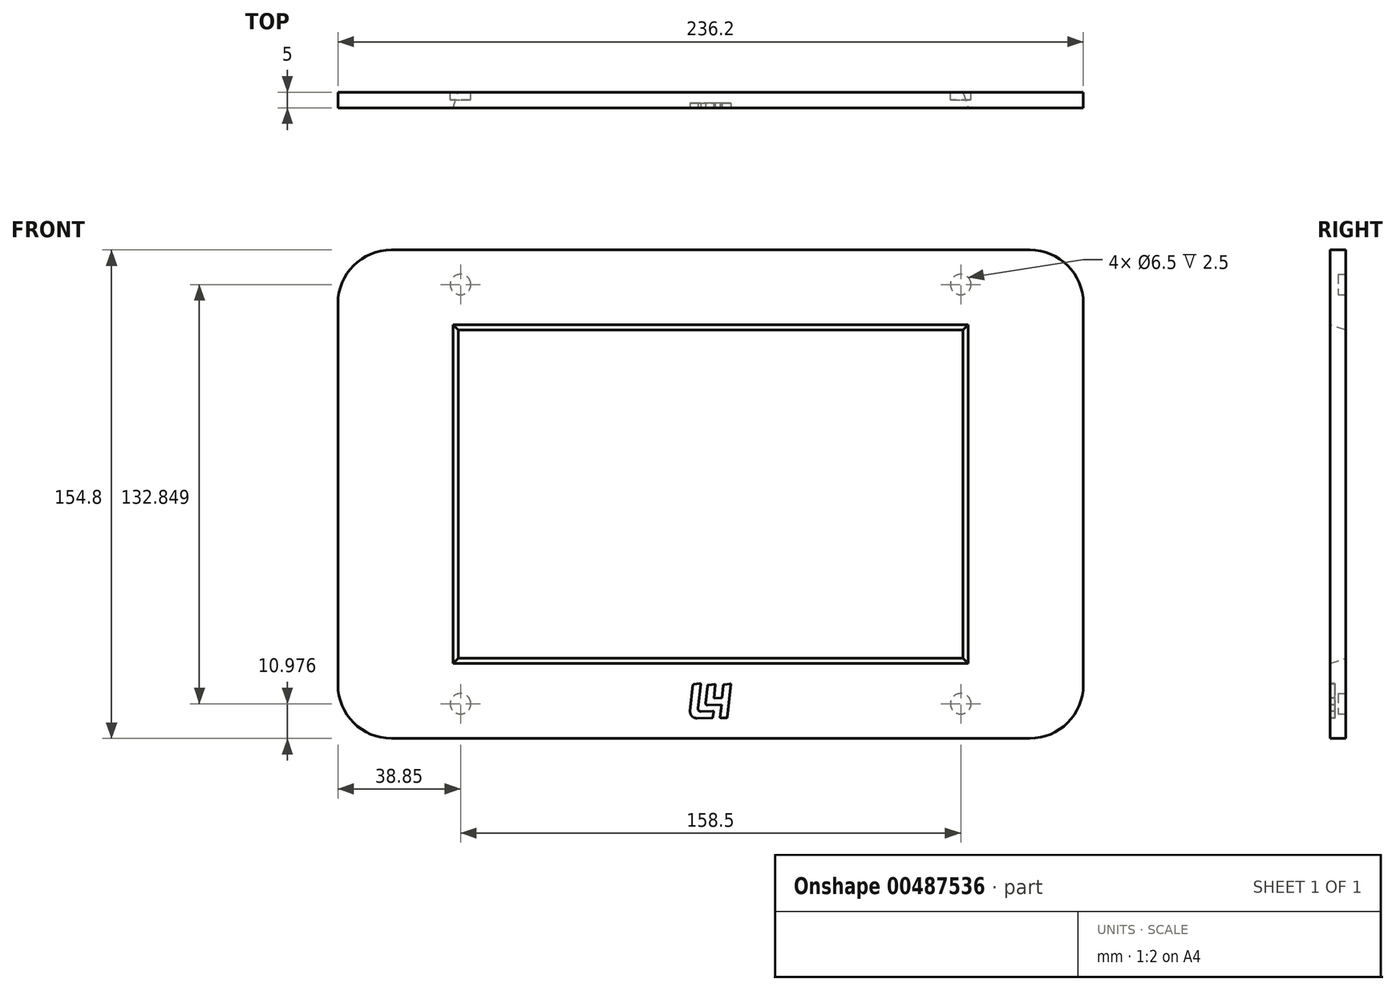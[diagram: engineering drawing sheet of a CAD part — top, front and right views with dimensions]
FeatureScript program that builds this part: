
annotation { "Feature Type Name" : "Feature", "Feature Type Description" : "" }
export const myFeature = defineFeature(function(context is Context, id is Id, definition is map)
    precondition{}
    {
        {
            var Q0;
            Q0=qCreatedBy(makeId("Front.planeOp"),FACE);
            var sketch = newSketch(context, id + "F0", { "sketchPlane" : qUnion([Q0])});
            skLineSegment(sketch, "E0.bottom", {"start": v(-80, 52) * mm, "end": v(80, 52) * mm});
            skLineSegment(sketch, "E0.top", {"start": v(-80, -52) * mm, "end": v(80, -52) * mm});
            skLineSegment(sketch, "E0.left", {"start": v(-80, 52) * mm, "end": v(-80, -52) * mm});
            skLineSegment(sketch, "E0.right", {"start": v(80, 52) * mm, "end": v(80, -52) * mm});
            skPoint(sketch, "E0.middle", {"position": v(0, 0) * mm});
            skLineSegment(sketch, "E1.bottom", {"start": v(-118.1, 77.4) * mm, "end": v(118.1, 77.4) * mm});
            skLineSegment(sketch, "E1.top", {"start": v(-118.1, -77.4) * mm, "end": v(118.1, -77.4) * mm});
            skLineSegment(sketch, "E1.left", {"start": v(-118.1, 77.4) * mm, "end": v(-118.1, -77.4) * mm});
            skLineSegment(sketch, "E1.right", {"start": v(118.1, 77.4) * mm, "end": v(118.1, -77.4) * mm});
            skSolve(sketch);
        }
        {
            var Q0;
            Q0=makeQuery(id+"F0.imprint","IMPRINT",FACE,{"disambiguationData":[TD([[makeQuery(id+"F0.imprint","IMPRINT",EDGE,{"derivedFrom":sQuery(id+"F0.wireOp",EDGE,"E0.bottom")}),1.0]])]});
            extrude(context, id + "F1", {"entities" : qUnion([Q0]), "depth" : 5 * mm});
        }
        {
            var Q0;
            Q0=makeQuery(id+"F1.opExtrude","SWEPT_EDGE",EDGE,{"disambiguationData":[OSD([sQuery(id+"F0.wireOp",EDGE,"E1.bottom"),sQuery(id+"F0.wireOp",EDGE,"E1.left")])]});
            var Q1;
            Q1=makeQuery(id+"F1.opExtrude","SWEPT_EDGE",EDGE,{"disambiguationData":[OSD([sQuery(id+"F0.wireOp",EDGE,"E1.bottom"),sQuery(id+"F0.wireOp",EDGE,"E1.right")])]});
            var Q2;
            Q2=makeQuery(id+"F1.opExtrude","SWEPT_EDGE",EDGE,{"disambiguationData":[OSD([sQuery(id+"F0.wireOp",EDGE,"E1.top"),sQuery(id+"F0.wireOp",EDGE,"E1.left")])]});
            var Q3;
            Q3=makeQuery(id+"F1.opExtrude","SWEPT_EDGE",EDGE,{"disambiguationData":[OSD([sQuery(id+"F0.wireOp",EDGE,"E1.top"),sQuery(id+"F0.wireOp",EDGE,"E1.right")])]});
            fillet(context, id + "F2", {"entities" : qUnion([Q0, Q1, Q2, Q3]), "radius" : 17 * mm, "tangentPropagation" : true, "allowEdgeOverflow" : false});
        }
        {
            var Q0;
            Q0=makeQuery(id+"F1.opExtrude","CAP_FACE",FACE,{"disambiguationData":[OSD([sQuery(id+"F0.wireOp",EDGE,"E0.bottom"),sQuery(id+"F0.wireOp",EDGE,"E0.top"),sQuery(id+"F0.wireOp",EDGE,"E0.left"),sQuery(id+"F0.wireOp",EDGE,"E0.right"),sQuery(id+"F0.wireOp",EDGE,"E1.bottom"),sQuery(id+"F0.wireOp",EDGE,"E1.top"),sQuery(id+"F0.wireOp",EDGE,"E1.left"),sQuery(id+"F0.wireOp",EDGE,"E1.right")])],"isStart":true});
            var sketch = newSketch(context, id + "F3", { "sketchPlane" : qUnion([Q0])});
            skCircle(sketch, "E2", {"center": v(-79.25, 66.42) * mm, "radius": 3.25 * mm});
            skCircle(sketch, "E3.MirrorC", {"center": v(-79.25, -66.42) * mm, "radius": 3.25 * mm});
            skCircle(sketch, "E4.MirrorC", {"center": v(79.25, 66.42) * mm, "radius": 3.25 * mm});
            skCircle(sketch, "E5.MirrorC", {"center": v(79.25, -66.42) * mm, "radius": 3.25 * mm});
            skSolve(sketch);
        }
        {
            var Q0;
            Q0=qSketchRegion(id+"F3",true);
            extrude(context, id + "F4", {"entities" : qUnion([Q0]), "operationType" : NewBodyOperationType.REMOVE, "oppositeDirection" : true, "depth" : 2.5 * mm});
        }
        {
            var Q0;
            Q0=makeQuery(id+"F1.opExtrude","CAP_EDGE",EDGE,{"disambiguationData":[OSD([sQuery(id+"F0.wireOp",EDGE,"E0.left")])],"isStart":false});
            var Q1;
            Q1=makeQuery(id+"F1.opExtrude","CAP_EDGE",EDGE,{"disambiguationData":[OSD([sQuery(id+"F0.wireOp",EDGE,"E0.bottom")])],"isStart":false});
            var Q2;
            Q2=makeQuery(id+"F1.opExtrude","CAP_EDGE",EDGE,{"disambiguationData":[OSD([sQuery(id+"F0.wireOp",EDGE,"E0.right")])],"isStart":false});
            var Q3;
            Q3=makeQuery(id+"F1.opExtrude","CAP_EDGE",EDGE,{"disambiguationData":[OSD([sQuery(id+"F0.wireOp",EDGE,"E0.top")])],"isStart":false});
            chamfer(context, id + "F5", {"entities" : qUnion([Q0, Q1, Q2, Q3]), "chamferType" : ChamferType.OFFSET_ANGLE, "width" : 5 * mm, "oppositeDirection" : false, "angle" : 18 * degree, "tangentPropagation" : true});
        }
        {
            var Q0;
            Q0=makeQuery(id+"F1.opExtrude","CAP_FACE",FACE,{"disambiguationData":[OSD([sQuery(id+"F0.wireOp",EDGE,"E0.bottom"),sQuery(id+"F0.wireOp",EDGE,"E0.top"),sQuery(id+"F0.wireOp",EDGE,"E0.left"),sQuery(id+"F0.wireOp",EDGE,"E0.right"),sQuery(id+"F0.wireOp",EDGE,"E1.bottom"),sQuery(id+"F0.wireOp",EDGE,"E1.top"),sQuery(id+"F0.wireOp",EDGE,"E1.left"),sQuery(id+"F0.wireOp",EDGE,"E1.right")])],"isStart":false});
            var sketch = newSketch(context, id + "F6", { "sketchPlane" : qUnion([Q0])});
            skPoint(sketch, "E6", {"position": v(0, -65.51) * mm});
            skPoint(sketch, "E6.positionSnap0", {"position": v(0, -75.04) * mm});
            skPoint(sketch, "E6.positionSnap1", {"position": v(10.5, -65.51) * mm});
            skLineSegment(sketch, "E7", {"start": v(0, -53.62) * mm, "end": v(0, -77.4) * mm});
            skLineSegment(sketch, "E8", {"start": v(-5.6, -60.55) * mm, "end": v(-6.49, -68.68) * mm});
            skLineSegment(sketch, "E9", {"start": v(-4.35, -71) * mm, "end": v(0.45, -70.9) * mm});
            skLineSegment(sketch, "E10", {"start": v(0.74, -70.63) * mm, "end": v(0.95, -68.94) * mm});
            skLineSegment(sketch, "E11", {"start": v(0.74, -68.71) * mm, "end": v(-3.13, -68.85) * mm});
            skLineSegment(sketch, "E12", {"start": v(-4, -67.9) * mm, "end": v(-3.09, -60.3) * mm});
            skLineSegment(sketch, "E13", {"start": v(-3.37, -60.02) * mm, "end": v(-5.35, -60.28) * mm});
            skPoint(sketch, "E14.visualSharp", {"position": v(-5.58, -60.32) * mm});
            skArc(sketch, "E14.filletArc", {"start": v(-5.35, -60.28) * mm, "mid": v(-5.52, -60.37) * mm, "end": v(-5.6, -60.55) * mm});
            skPoint(sketch, "E15.visualSharp", {"position": v(-3.05, -59.98) * mm});
            skArc(sketch, "E15.filletArc", {"start": v(-3.09, -60.3) * mm, "mid": v(-3.16, -60.1) * mm, "end": v(-3.37, -60.02) * mm});
            skPoint(sketch, "E16.visualSharp", {"position": v(-6.74, -71.06) * mm});
            skArc(sketch, "E16.filletArc", {"start": v(-6.49, -68.68) * mm, "mid": v(-5.95, -70.33) * mm, "end": v(-4.35, -71) * mm});
            skPoint(sketch, "E17.visualSharp", {"position": v(0.98, -68.7) * mm});
            skArc(sketch, "E17.filletArc", {"start": v(0.95, -68.94) * mm, "mid": v(0.9, -68.78) * mm, "end": v(0.74, -68.71) * mm});
            skPoint(sketch, "E18.visualSharp", {"position": v(0.71, -70.89) * mm});
            skArc(sketch, "E18.filletArc", {"start": v(0.45, -70.9) * mm, "mid": v(0.65, -70.82) * mm, "end": v(0.74, -70.63) * mm});
            skPoint(sketch, "E19.visualSharp", {"position": v(-4.12, -68.88) * mm});
            skArc(sketch, "E19.filletArc", {"start": v(-4, -67.9) * mm, "mid": v(-3.78, -68.57) * mm, "end": v(-3.13, -68.85) * mm});
            skLineSegment(sketch, "E20", {"start": v(-0.98, -60.7) * mm, "end": v(-1.55, -66.23) * mm});
            skLineSegment(sketch, "E21", {"start": v(3.43, -66.69) * mm, "end": v(-0.93, -66.9) * mm});
            skLineSegment(sketch, "E22", {"start": v(3.43, -66.69) * mm, "end": v(3.03, -70.63) * mm});
            skLineSegment(sketch, "E23", {"start": v(3.23, -70.85) * mm, "end": v(5.05, -70.85) * mm});
            skLineSegment(sketch, "E24", {"start": v(5.25, -70.68) * mm, "end": v(6.44, -60.28) * mm});
            skLineSegment(sketch, "E25", {"start": v(6.2, -60.06) * mm, "end": v(4.28, -60.35) * mm});
            skLineSegment(sketch, "E26", {"start": v(4.03, -60.62) * mm, "end": v(3.63, -64.5) * mm});
            skLineSegment(sketch, "E27", {"start": v(3.63, -64.5) * mm, "end": v(1.02, -64.62) * mm});
            skLineSegment(sketch, "E28", {"start": v(1.02, -64.62) * mm, "end": v(1.5, -60.49) * mm});
            skLineSegment(sketch, "E29", {"start": v(1.3, -60.27) * mm, "end": v(-0.7, -60.43) * mm});
            skPoint(sketch, "E30.visualSharp", {"position": v(-0.95, -60.45) * mm});
            skArc(sketch, "E30.filletArc", {"start": v(-0.7, -60.43) * mm, "mid": v(-0.9, -60.51) * mm, "end": v(-0.98, -60.7) * mm});
            skPoint(sketch, "E31.visualSharp", {"position": v(1.54, -60.25) * mm});
            skArc(sketch, "E31.filletArc", {"start": v(1.5, -60.49) * mm, "mid": v(1.45, -60.33) * mm, "end": v(1.3, -60.27) * mm});
            skPoint(sketch, "E32.visualSharp", {"position": v(-1.62, -66.93) * mm});
            skArc(sketch, "E32.filletArc", {"start": v(-1.55, -66.23) * mm, "mid": v(-1.4, -66.7) * mm, "end": v(-0.93, -66.9) * mm});
            skPoint(sketch, "E33.visualSharp", {"position": v(3, -70.85) * mm});
            skArc(sketch, "E33.filletArc", {"start": v(3.03, -70.63) * mm, "mid": v(3.08, -70.79) * mm, "end": v(3.23, -70.85) * mm});
            skPoint(sketch, "E34.visualSharp", {"position": v(5.23, -70.85) * mm});
            skArc(sketch, "E34.filletArc", {"start": v(5.05, -70.85) * mm, "mid": v(5.18, -70.8) * mm, "end": v(5.25, -70.68) * mm});
            skPoint(sketch, "E35.visualSharp", {"position": v(6.47, -60.02) * mm});
            skArc(sketch, "E35.filletArc", {"start": v(6.44, -60.28) * mm, "mid": v(6.38, -60.11) * mm, "end": v(6.2, -60.06) * mm});
            skPoint(sketch, "E36.visualSharp", {"position": v(4.05, -60.39) * mm});
            skArc(sketch, "E36.filletArc", {"start": v(4.28, -60.35) * mm, "mid": v(4.1, -60.44) * mm, "end": v(4.03, -60.62) * mm});
            skSolve(sketch);
        }
        {
            var Q0;
            Q0=makeQuery(id+"F6.imprint","IMPRINT",FACE,{"disambiguationData":[TD([[makeQuery(id+"F6.imprint","IMPRINT",EDGE,{"derivedFrom":sQuery(id+"F6.wireOp",EDGE,"E8")}),1.0]])]});
            var Q1;
            {var subQ6=sQuery(id+"F6.wireOp",EDGE,"E22");Q1=makeQuery(id+"F6.imprint","IMPRINT",FACE,{"disambiguationData":[TD([[makeQuery(id+"F6.imprint","IMPRINT",EDGE,{"derivedFrom":subQ6}),1.0]])]});}
            var Q2;
            Q2=makeQuery(id+"F6.imprint","IMPRINT",FACE,{"disambiguationData":[TD([[makeQuery(id+"F6.imprint","IMPRINT",EDGE,{"derivedFrom":sQuery(id+"F6.wireOp",EDGE,"E20")}),1.0]])]});
            var Q3;
            Q3=makeQuery(id+"F6.imprint","IMPRINT",FACE,{"disambiguationData":[TD([[makeQuery(id+"F6.imprint","IMPRINT",EDGE,{"derivedFrom":sQuery(id+"F6.wireOp",EDGE,"E10")}),1.0]])]});
            extrude(context, id + "F7", {"entities" : qUnion([Q0, Q1, Q2, Q3]), "operationType" : NewBodyOperationType.REMOVE, "oppositeDirection" : true, "depth" : 1.5 * mm});
        }
    });
